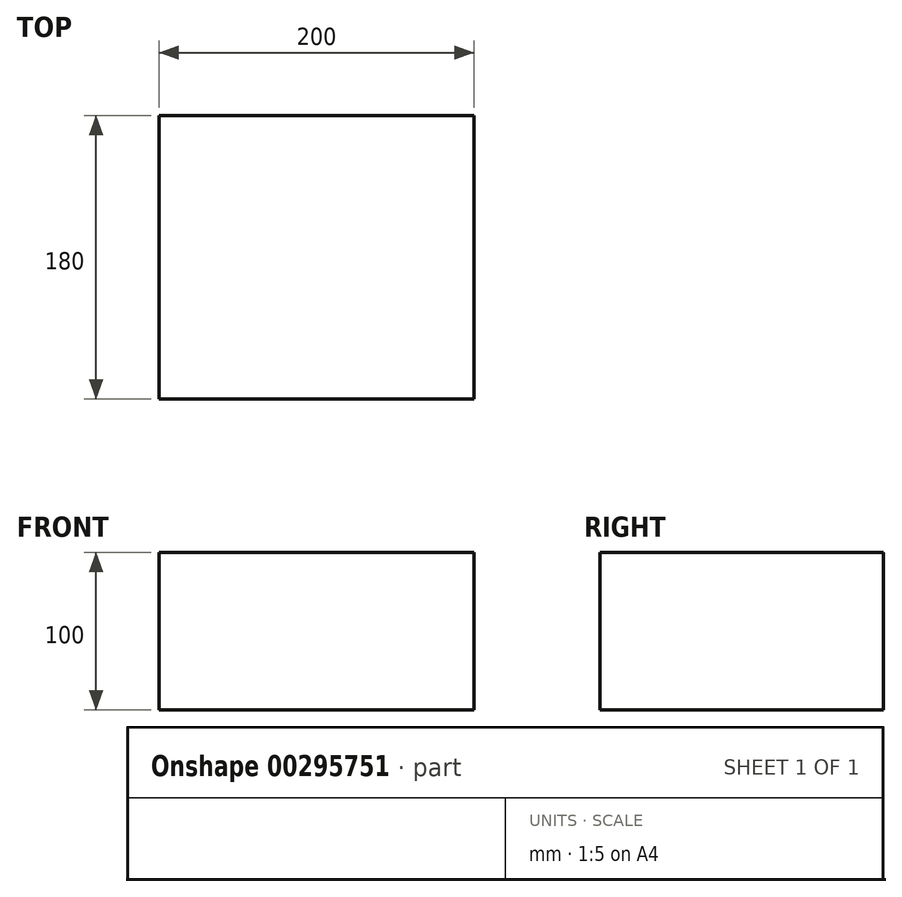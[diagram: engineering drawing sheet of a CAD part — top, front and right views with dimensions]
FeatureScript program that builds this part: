
annotation { "Feature Type Name" : "Feature", "Feature Type Description" : "" }
export const myFeature = defineFeature(function(context is Context, id is Id, definition is map)
    precondition{}
    {
        {
            var Q0;
            Q0=qCreatedBy(makeId("Top.planeOp"),FACE);
            var sketch = newSketch(context, id + "F0", { "sketchPlane" : qUnion([Q0])});
            skLineSegment(sketch, "E0.bottom", {"start": v(-115.9, 107.86) * mm, "end": v(84.1, 107.86) * mm});
            skLineSegment(sketch, "E0.top", {"start": v(-115.9, -72.14) * mm, "end": v(84.1, -72.14) * mm});
            skLineSegment(sketch, "E0.left", {"start": v(-115.9, 107.86) * mm, "end": v(-115.9, -72.14) * mm});
            skLineSegment(sketch, "E0.right", {"start": v(84.1, 107.86) * mm, "end": v(84.1, -72.14) * mm});
            skSolve(sketch);
        }
        {
            var Q0;
            Q0=makeQuery(id+"F0.imprint","IMPRINT",FACE,{"disambiguationData":[TD([[makeQuery(id+"F0.imprint","IMPRINT",EDGE,{"derivedFrom":sQuery(id+"F0.wireOp",EDGE,"E0.bottom")}),-1.0]])]});
            extrude(context, id + "F1", {"entities" : qUnion([Q0]), "depth" : 100 * mm});
        }
    });
